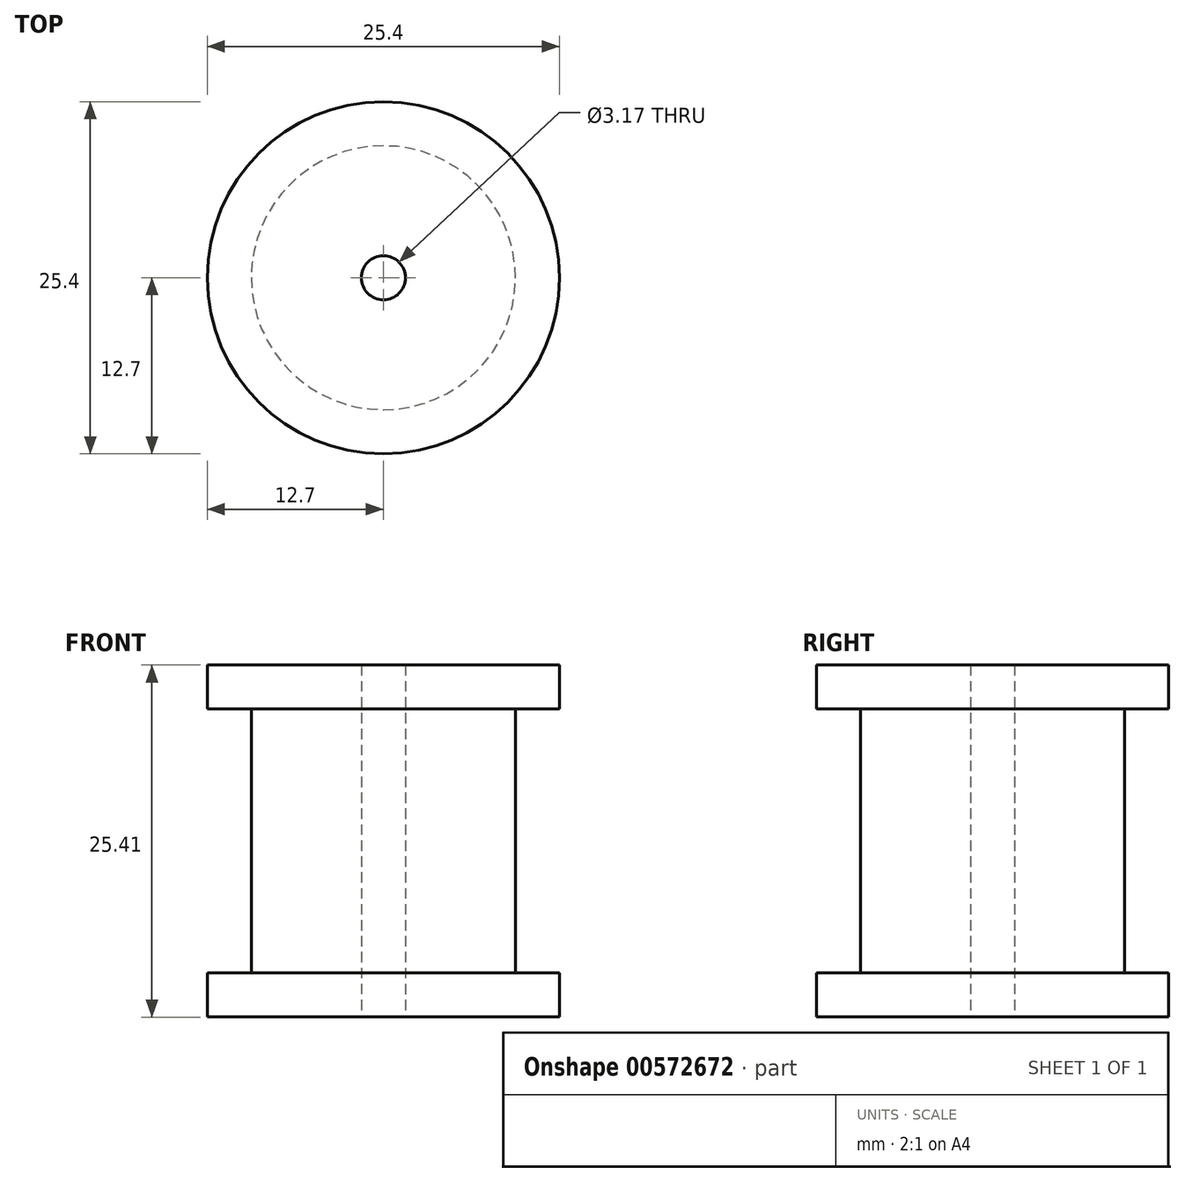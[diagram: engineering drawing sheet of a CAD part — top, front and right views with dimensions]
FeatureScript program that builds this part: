
annotation { "Feature Type Name" : "Feature", "Feature Type Description" : "" }
export const myFeature = defineFeature(function(context is Context, id is Id, definition is map)
    precondition{}
    {
        {
            var Q0;
            Q0=qCreatedBy(makeId("Top.planeOp"),FACE);
            var sketch = newSketch(context, id + "F0", { "sketchPlane" : qUnion([Q0])});
            skCircle(sketch, "E0", {"center": v(0, 0) * mm, "radius": 9.53 * mm});
            skSolve(sketch);
        }
        {
            var Q0;
            Q0=makeQuery(id+"F0.imprint","IMPRINT",FACE,{"disambiguationData":[TD([[makeQuery(id+"F0.imprint","IMPRINT",EDGE,{"derivedFrom":sQuery(id+"F0.wireOp",EDGE,"E0")}),1.0]])]});
            extrude(context, id + "F1", {"entities" : qUnion([Q0]), "depth" : 19.05 * mm, "offsetDistance" : 25.4 * mm});
        }
        {
            var Q0;
            Q0=qCreatedBy(makeId("Top.planeOp"),FACE);
            var sketch = newSketch(context, id + "F2", { "sketchPlane" : qUnion([Q0])});
            skCircle(sketch, "E1", {"center": v(0, 0) * mm, "radius": 12.7 * mm});
            skSolve(sketch);
        }
        {
            var Q0;
            Q0=makeQuery(id+"F2.imprint","IMPRINT",FACE,{"disambiguationData":[TD([[makeQuery(id+"F2.imprint","IMPRINT",EDGE,{"derivedFrom":sQuery(id+"F2.wireOp",EDGE,"E1")}),1.0]])]});
            var Q1;
            Q1=sQuery(id+"F2.wireOp",EDGE,"E1");
            extrude(context, id + "F3", {"entities" : qUnion([Q0]), "operationType" : NewBodyOperationType.ADD, "surfaceEntities" : qUnion([Q1]), "oppositeDirection" : true, "depth" : 3.17 * mm, "offsetDistance" : 25.4 * mm});
        }
        {
            var Q0;
            Q0=makeQuery(id+"F1.opExtrude","CAP_FACE",FACE,{"disambiguationData":[OSD([sQuery(id+"F0.wireOp",EDGE,"E0")])],"isStart":false});
            var sketch = newSketch(context, id + "F4", { "sketchPlane" : qUnion([Q0])});
            skCircle(sketch, "E2", {"center": v(0, 0) * mm, "radius": 12.7 * mm});
            skSolve(sketch);
        }
        {
            var Q0;
            Q0=makeQuery(id+"F4.imprint","IMPRINT",FACE,{"disambiguationData":[TD([[makeQuery(id+"F4.imprint","IMPRINT",EDGE,{"derivedFrom":sQuery(id+"F4.wireOp",EDGE,"E2")}),1.0]])]});
            var Q1;
            Q1=makeQuery(id+"F4.imprint","IMPRINT",FACE,{"disambiguationData":[TD([[makeQuery(id+"F4.imprint","IMPRINT",EDGE,{"derivedFrom":makeQuery(id+"F1.opExtrude","CAP_EDGE",EDGE,{"disambiguationData":[OSD([sQuery(id+"F0.wireOp",EDGE,"E0")])],"isStart":false})}),1.0]])]});
            var Q2;
            Q2=sQuery(id+"F4.wireOp",EDGE,"E2");
            extrude(context, id + "F5", {"entities" : qUnion([Q0, Q1]), "operationType" : NewBodyOperationType.ADD, "surfaceEntities" : qUnion([Q2]), "depth" : 3.17 * mm, "offsetDistance" : 25.4 * mm});
        }
        {
            var Q0;
            Q0=qCreatedBy(makeId("Top.planeOp"),FACE);
            var sketch = newSketch(context, id + "F6", { "sketchPlane" : qUnion([Q0])});
            skCircle(sketch, "E3", {"center": v(0, 0) * mm, "radius": 1.59 * mm});
            skSolve(sketch);
        }
        {
            var Q0;
            Q0 = qSketchRegion(id + "F6", true);
            extrude(context, id + "F7", {"entities" : qUnion([Q0]), "operationType" : NewBodyOperationType.REMOVE, "endBound" : BoundingType.SYMMETRIC, "depth" : 50.8 * mm, "offsetDistance" : 25.4 * mm});
        }
    });
